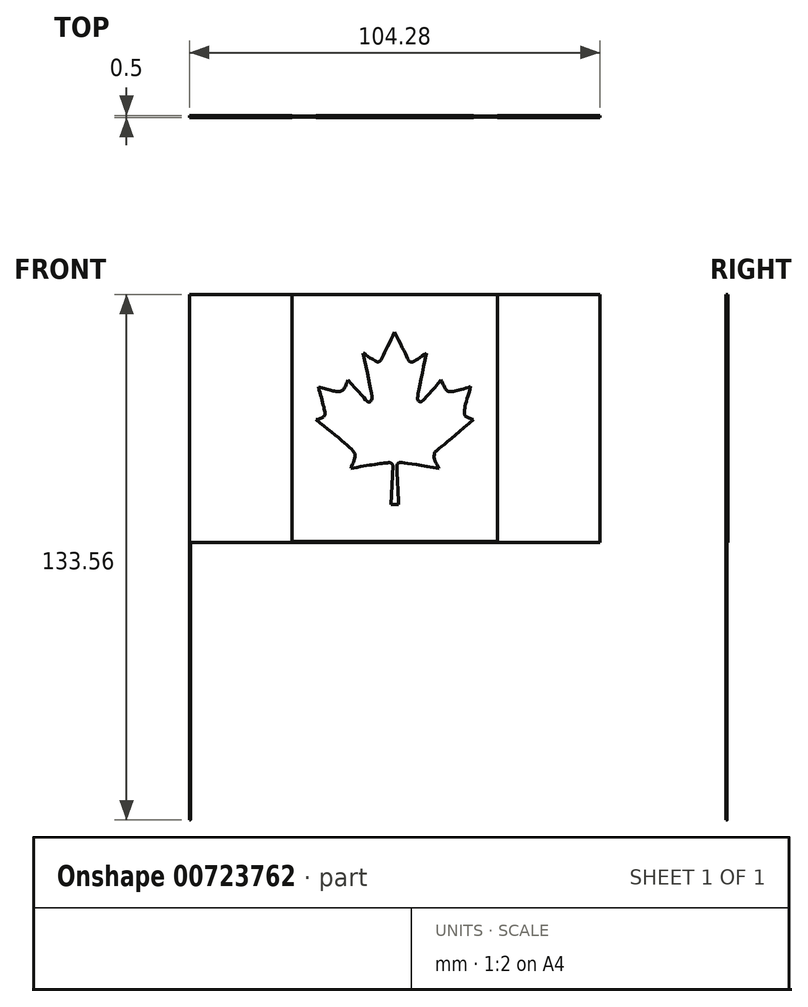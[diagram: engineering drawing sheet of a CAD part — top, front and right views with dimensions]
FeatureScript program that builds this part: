
annotation { "Feature Type Name" : "Feature", "Feature Type Description" : "" }
export const myFeature = defineFeature(function(context is Context, id is Id, definition is map)
    precondition{}
    {
        {
            var Q0;
            Q0=qCreatedBy(makeId("Front.planeOp"),FACE);
            var sketch = newSketch(context, id + "F0", { "sketchPlane" : qUnion([Q0])});
            skLineSegment(sketch, "E0", {"start": v(0, -21.38) * mm, "end": v(-1, -21.38) * mm});
            skLineSegment(sketch, "E1", {"start": v(-1, -21.38) * mm, "end": v(-0.5, -11.55) * mm});
            skPoint(sketch, "E1.endSnap0", {"position": v(-0.5, -21.38) * mm});
            skFitSpline(sketch, "E2", {"points": [v(-0.5, -11.55) * mm, v(-0.74, -10.97) * mm, v(-1.62, -10.79) * mm, v(-11.14, -12.22) * mm], "startDerivative": vector(-1.14, 4.37) * mm, "endDerivative": vector(-18.65, -3.22) * mm});
            skFitSpline(sketch, "E3", {"points": [v(-11.14, -12.22) * mm, v(-10.07, -9.28) * mm, v(-10.4, -8.04) * mm, v(-19.97, 0.13) * mm], "startDerivative": vector(5.1, 12.16) * mm, "endDerivative": vector(-22.99, 18.15) * mm});
            skFitSpline(sketch, "E4", {"points": [v(-19.97, 0.13) * mm, v(-17.95, 1) * mm, v(-17.72, 1.79) * mm, v(-19.37, 8.4) * mm], "startDerivative": vector(8.41, 2.77) * mm, "endDerivative": vector(-4.44, 15.7) * mm});
            skFitSpline(sketch, "E5", {"points": [v(-19.37, 8.4) * mm, v(-15.16, 7.37) * mm, v(-13.34, 7.54) * mm, v(-11.88, 10.27) * mm], "startDerivative": vector(11.44, -3.07) * mm, "endDerivative": vector(3.73, 10.06) * mm});
            skFitSpline(sketch, "E6", {"points": [v(-11.88, 10.27) * mm, v(-6.99, 4.83) * mm, v(-6.8, 4.72) * mm, v(-6.39, 4.68) * mm, v(-5.97, 5) * mm, v(-5.8, 5.43) * mm, v(-8.08, 17.05) * mm], "startDerivative": vector(21.11, -24.04) * mm, "endDerivative": vector(-8.9, 39.35) * mm});
            skFitSpline(sketch, "E7", {"points": [v(-8.08, 17.05) * mm, v(-4.66, 14.94) * mm, v(-4.25, 14.84) * mm, v(-3.83, 14.92) * mm, v(-3.42, 15.48) * mm, v(0, 22.41) * mm], "startDerivative": vector(14.76, -9.56) * mm, "endDerivative": vector(10.7, 21.83) * mm});
            skFitSpline(sketch, "E8", {"points": [v(0, 22.41) * mm, v(3.6, 15.15) * mm, v(3.81, 14.9) * mm, v(4.17, 14.79) * mm, v(4.82, 14.97) * mm, v(8.09, 17.05) * mm], "startDerivative": vector(11.43, -23.33) * mm, "endDerivative": vector(13.44, 9.06) * mm});
            skFitSpline(sketch, "E9", {"points": [v(8.09, 17.05) * mm, v(5.82, 5.8) * mm, v(5.85, 5.36) * mm, v(6.03, 4.93) * mm, v(6.57, 4.7) * mm, v(7.31, 5.16) * mm, v(11.77, 10.27) * mm], "startDerivative": vector(-8.68, -40.36) * mm, "endDerivative": vector(18.66, 22.14) * mm});
            skFitSpline(sketch, "E10", {"points": [v(11.77, 10.27) * mm, v(12.8, 8.12) * mm, v(13.42, 7.45) * mm, v(14.58, 7.3) * mm, v(19.3, 8.53) * mm], "startDerivative": vector(4.09, -9.11) * mm, "endDerivative": vector(14.26, 4.4) * mm});
            skFitSpline(sketch, "E11", {"points": [v(19.3, 8.53) * mm, v(17.73, 2.66) * mm, v(17.76, 1.54) * mm, v(17.95, 1.06) * mm, v(18.95, 0.56) * mm, v(20.02, 0.13) * mm], "startDerivative": vector(-5.5, -18.01) * mm, "endDerivative": vector(6.1, -2.51) * mm});
            skFitSpline(sketch, "E12", {"points": [v(20.02, 0.13) * mm, v(10.78, -7.6) * mm, v(10.34, -8) * mm, v(10.07, -8.63) * mm, v(10.17, -10.1) * mm, v(11.24, -12.22) * mm], "startDerivative": vector(-27.53, -23.2) * mm, "endDerivative": vector(6.55, -10.86) * mm});
            skFitSpline(sketch, "E13", {"points": [v(11.24, -12.22) * mm, v(1.67, -10.77) * mm, v(1.06, -10.82) * mm, v(0.68, -11.12) * mm, v(0.54, -12.22) * mm, v(1, -21.38) * mm], "startDerivative": vector(-34.76, 5.69) * mm, "endDerivative": vector(1.8, -32.37) * mm});
            skLineSegment(sketch, "E14", {"start": v(1, -21.38) * mm, "end": v(0, -21.38) * mm});
            skLineSegment(sketch, "E15", {"start": v(-52.13, 31.96) * mm, "end": v(52.15, 31.96) * mm});
            skLineSegment(sketch, "E16", {"start": v(52.15, 31.96) * mm, "end": v(52.15, -31) * mm});
            skLineSegment(sketch, "E17", {"start": v(52.15, -31) * mm, "end": v(-52.13, -31) * mm});
            skLineSegment(sketch, "E18", {"start": v(-52.13, -31) * mm, "end": v(-52.13, 31.96) * mm});
            skLineSegment(sketch, "E19", {"start": v(-26.11, 31.96) * mm, "end": v(-26.11, -31) * mm});
            skLineSegment(sketch, "E20", {"start": v(26.13, 31.96) * mm, "end": v(26.13, -31) * mm});
            skSolve(sketch);
        }
        {
            var Q0;
            Q0=makeQuery(id+"F0.imprint","IMPRINT",FACE,{"disambiguationData":[TD([[makeQuery(id+"F0.imprint","IMPRINT",EDGE,{"derivedFrom":sQuery(id+"F0.wireOp",EDGE,"E0")}),-1.0]])]});
            var Q1;
            {var subQ0=sQuery(id+"F0.wireOp",EDGE,"E18");Q1=makeQuery(id+"F0.imprint","IMPRINT",FACE,{"disambiguationData":[TD([[makeQuery(id+"F0.imprint","IMPRINT",EDGE,{"derivedFrom":subQ0}),-1.0]])]});}
            var Q2;
            {var subQ0=sQuery(id+"F0.wireOp",EDGE,"E16");Q2=makeQuery(id+"F0.imprint","IMPRINT",FACE,{"disambiguationData":[TD([[makeQuery(id+"F0.imprint","IMPRINT",EDGE,{"derivedFrom":subQ0}),-1.0]])]});}
            extrude(context, id + "F1", {"entities" : qUnion([Q0, Q1, Q2]), "endBound" : BoundingType.SYMMETRIC, "depth" : 0.5 * mm, "offsetDistance" : 25.4 * mm});
        }
        {
            var Q0;
            Q0=qCreatedBy(makeId("Front.planeOp"),FACE);
            var sketch = newSketch(context, id + "F2", { "sketchPlane" : qUnion([Q0])});
            skLineSegment(sketch, "E21", {"start": v(-26.11, 31.96) * mm, "end": v(26.13, 31.96) * mm});
            skLineSegment(sketch, "E22", {"start": v(26.13, 31.96) * mm, "end": v(26.13, 31.9) * mm});
            skLineSegment(sketch, "E23", {"start": v(26.13, 31.9) * mm, "end": v(-26.11, 31.9) * mm});
            skLineSegment(sketch, "E24", {"start": v(-26.11, 31.9) * mm, "end": v(-26.11, 31.96) * mm});
            skLineSegment(sketch, "E25", {"start": v(-26.11, -31) * mm, "end": v(26.13, -31) * mm});
            skLineSegment(sketch, "E26", {"start": v(26.13, -31) * mm, "end": v(26.13, -31) * mm});
            skLineSegment(sketch, "E27", {"start": v(26.13, -31) * mm, "end": v(26.13, -30.75) * mm});
            skLineSegment(sketch, "E28", {"start": v(26.13, -30.75) * mm, "end": v(-26.11, -30.75) * mm});
            skLineSegment(sketch, "E29", {"start": v(-26.11, -30.75) * mm, "end": v(-26.11, -31) * mm});
            skSolve(sketch);
        }
        {
            var Q0;
            Q0 = qSketchRegion(id + "F2", true);
            extrude(context, id + "F3", {"entities" : qUnion([Q0]), "operationType" : NewBodyOperationType.ADD, "depth" : 0.03 * mm, "offsetDistance" : 25.4 * mm});
        }
        {
            var Q0;
            Q0=qCreatedBy(makeId("Top.planeOp"),FACE);
            var sketch = newSketch(context, id + "F4", { "sketchPlane" : qUnion([Q0])});
            skCircle(sketch, "E30", {"center": v(-52, -0.13) * mm, "radius": 0.13 * mm});
            skSolve(sketch);
        }
        {
            var Q0;
            Q0 = qSketchRegion(id + "F4", true);
            extrude(context, id + "F5", {"entities" : qUnion([Q0]), "operationType" : NewBodyOperationType.ADD, "oppositeDirection" : true, "depth" : 101.6 * mm, "offsetDistance" : 25.4 * mm});
        }
        {
            var Q0;
            Q0=qCreatedBy(makeId("Front.planeOp"),FACE);
            var sketch = newSketch(context, id + "F6", { "sketchPlane" : qUnion([Q0])});
            skLineSegment(sketch, "E31.bottom", {"start": v(-26.17, 31.9) * mm, "end": v(26.13, 31.9) * mm});
            skLineSegment(sketch, "E31.top", {"start": v(-26.17, -30.77) * mm, "end": v(26.13, -30.77) * mm});
            skLineSegment(sketch, "E31.left", {"start": v(-26.17, 31.9) * mm, "end": v(-26.17, -30.77) * mm});
            skLineSegment(sketch, "E31.right", {"start": v(26.13, 31.9) * mm, "end": v(26.13, -30.77) * mm});
            skSolve(sketch);
        }
        {
            var Q0;
            Q0=makeQuery(id+"F6.imprint","IMPRINT",FACE,{"disambiguationData":[TD([[makeQuery(id+"F6.imprint","IMPRINT",EDGE,{"derivedFrom":sQuery(id+"F6.wireOp",EDGE,"E31.bottom")}),-1.0]])]});
            extrude(context, id + "F7", {"entities" : qUnion([Q0]), "endBound" : BoundingType.SYMMETRIC, "depth" : 0.25 * mm, "offsetDistance" : 25.4 * mm});
        }
    });
